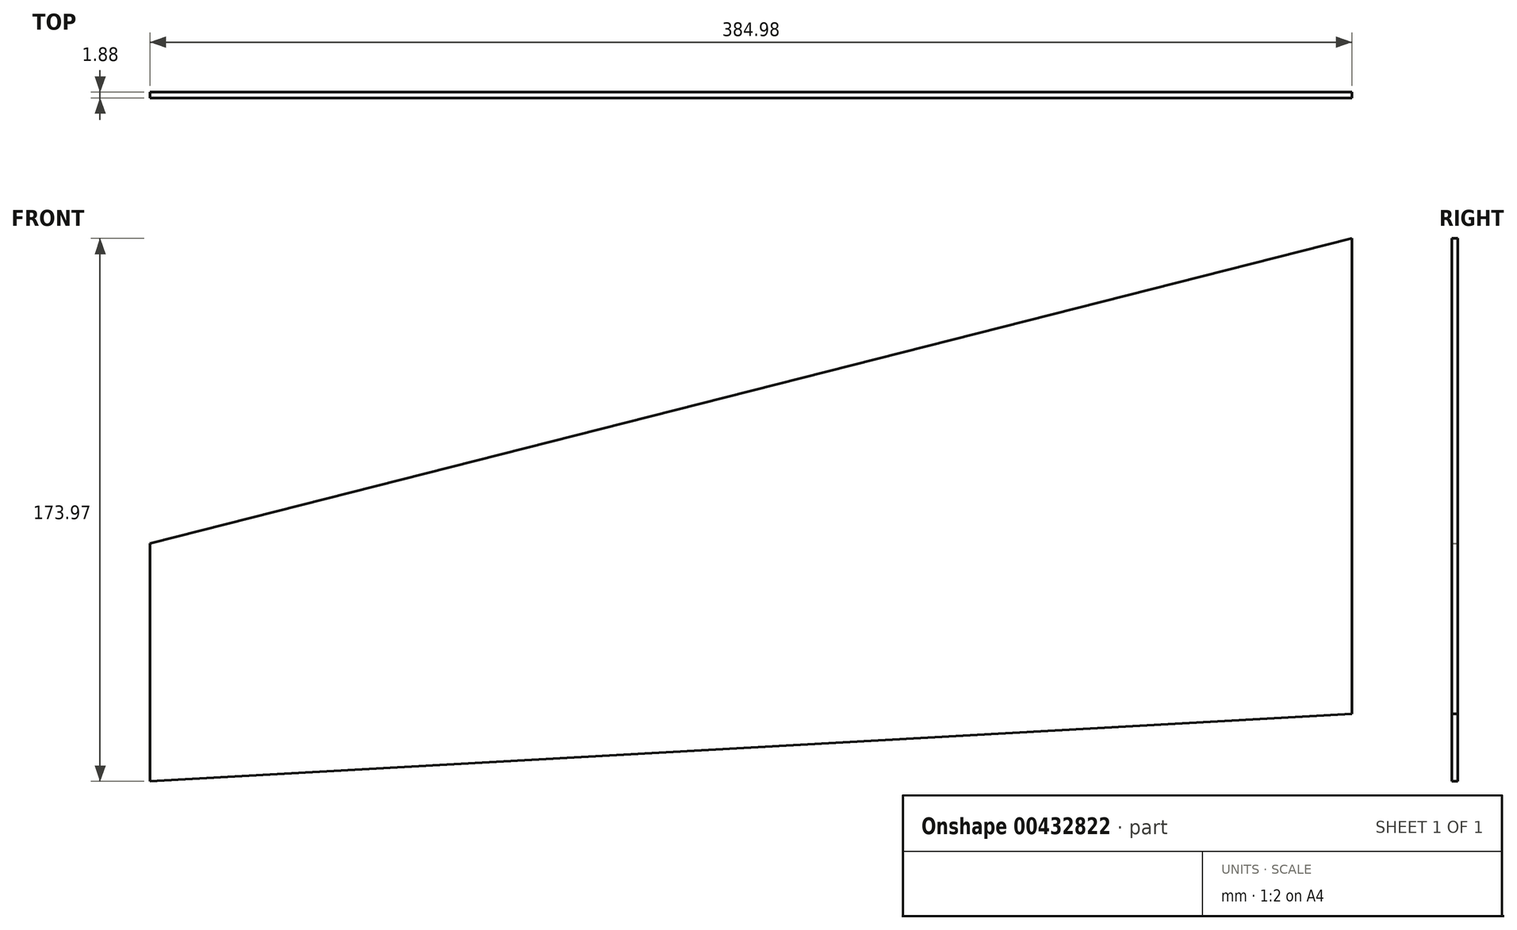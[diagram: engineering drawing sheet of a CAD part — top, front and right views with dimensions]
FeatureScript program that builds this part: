
annotation { "Feature Type Name" : "Feature", "Feature Type Description" : "" }
export const myFeature = defineFeature(function(context is Context, id is Id, definition is map)
    precondition{}
    {
        {
            var Q0;
            Q0=qCreatedBy(makeId("Front.planeOp"),FACE);
            var sketch = newSketch(context, id + "F0", { "sketchPlane" : qUnion([Q0])});
            skLineSegment(sketch, "E0.bottom", {"start": v(0, 0) * mm, "end": v(-384.98, -21.57) * mm});
            skLineSegment(sketch, "E0.left", {"start": v(0, 0) * mm, "end": v(0, 152.4) * mm});
            skLineSegment(sketch, "E0.right", {"start": v(-384.98, -21.57) * mm, "end": v(-384.98, 54.63) * mm});
            skLineSegment(sketch, "E1", {"start": v(0, 152.4) * mm, "end": v(-384.98, 54.63) * mm});
            skSolve(sketch);
        }
        {
            var Q0;
            Q0 = qSketchRegion(id + "F0", true);
            extrude(context, id + "F1", {"entities" : qUnion([Q0]), "depth" : 1.88 * mm});
        }
    });
